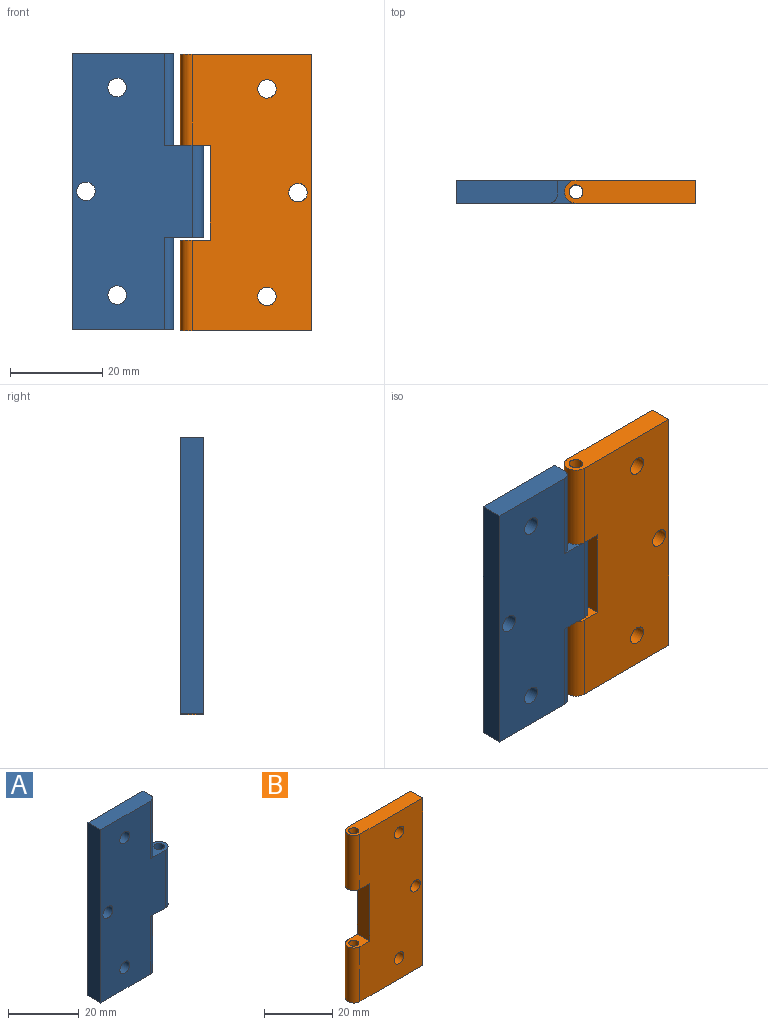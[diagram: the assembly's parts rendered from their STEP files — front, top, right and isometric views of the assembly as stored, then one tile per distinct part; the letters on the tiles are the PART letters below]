
ASSEMBLY  parts=2 mates=1
PART A: 16 faces, bbox 28.5x5x60 mm
  f0: plane 8.5x5mm, normal (0,0,1), area 23.6mm2, adj f1,f2,f3,f5,f7,f15
  f1: plane 60x26mm, normal (0,-1,0), area 1282.3mm2, adj f0,f2,f4,f6,f8,f10,f11,f12
  f2: cylinder r=2.5mm len=20mm, axis (0,0,-1), area 157.1mm2, adj f0,f1,f3,f6
  f3: plane 60x26mm, normal (0,1,0), area 1362.3mm2, adj f0,f2,f4,f6,f7,f8,f9,f10
  f4: plane 60x5mm, normal (-1,0,0), area 300mm2, adj f1,f3,f8,f10
  f5: cylinder r=1.5mm len=20mm, axis (0,0,-1), area 188.5mm2, adj f0,f6
  f6: plane 8.5x5mm, normal (0,0,-1), area 23.6mm2, adj f1,f2,f3,f5,f9,f14
  f7: plane 20x3mm, normal (1,0,0), area 60mm2, adj f0,f3,f8,f15
  f8: plane 22x5mm, normal (0,0,1), area 109.1mm2, adj f1,f3,f4,f7,f15
  f9: plane 20x3mm, normal (1,0,0), area 60mm2, adj f3,f6,f10,f14
  f10: plane 22x5mm, normal (0,0,-1), area 109.1mm2, adj f1,f3,f4,f9,f14
  f11: cylinder r=2mm len=5mm, axis (0,-1,0), area 62.8mm2, adj f1,f3
  f12: cylinder r=2mm len=5mm, axis (0,-1,0), area 62.8mm2, adj f1,f3
  f13: cylinder r=2mm len=5mm, axis (0,-1,0), area 62.8mm2, adj f1,f3
  f14: cylinder r=2mm len=20mm, axis (0,0,-1), area 62.8mm2, adj f1,f6,f9,f10
  f15: cylinder r=2mm len=20mm, axis (0,0,1), area 62.8mm2, adj f0,f1,f7,f8
PART B: 15 faces, bbox 28.5x5x60 mm
  f0: plane 60x26mm, normal (0,-1,0), area 1439.9mm2, adj f1,f4,f5,f6,f7,f9,f10,f11
  f1: cylinder r=2.5mm len=19.7mm, axis (0,0,-1), area 154.7mm2, adj f0,f3,f5,f14
  f2: cylinder r=1.5mm len=19.7mm, axis (0,0,-1), area 185.7mm2, adj f5,f14
  f3: plane 60x26mm, normal (0,1,0), area 1439.9mm2, adj f1,f4,f5,f6,f7,f9,f10,f11
  f4: plane 60x5mm, normal (1,0,0), area 300mm2, adj f0,f3,f5,f9
  f5: plane 28.5x5mm, normal (0,0,-1), area 132.7mm2, adj f0,f1,f2,f3,f4
  f6: plane 20.6x5mm, normal (-1,0,0), area 103mm2, adj f0,f3,f13,f14
  f7: cylinder r=2.5mm len=19.7mm, axis (0,0,-1), area 154.7mm2, adj f0,f3,f9,f13
  f8: cylinder r=1.5mm len=19.7mm, axis (0,0,-1), area 185.7mm2, adj f9,f13
  f9: plane 28.5x5mm, normal (0,0,1), area 132.7mm2, adj f0,f3,f4,f7,f8
  f10: cylinder r=2mm len=5mm, axis (0,-1,0), area 62.8mm2, adj f0,f3
  f11: cylinder r=2mm len=5mm, axis (0,-1,0), area 62.8mm2, adj f0,f3
  f12: cylinder r=2mm len=5mm, axis (0,-1,0), area 62.8mm2, adj f0,f3
  f13: plane 6.5x5mm, normal (0,0,-1), area 22.7mm2, adj f0,f3,f6,f7,f8
  f14: plane 6.5x5mm, normal (0,0,1), area 22.7mm2, adj f0,f1,f2,f3,f6
PLACE A t=(14.82,2.35,-0.2)mm
PLACE B t=(14.82,2.35,-0.5)mm
MATE revolute A.f5 <-> B.f2  axis (0,0,-1) through (14.82,2.35,39.8)mm
